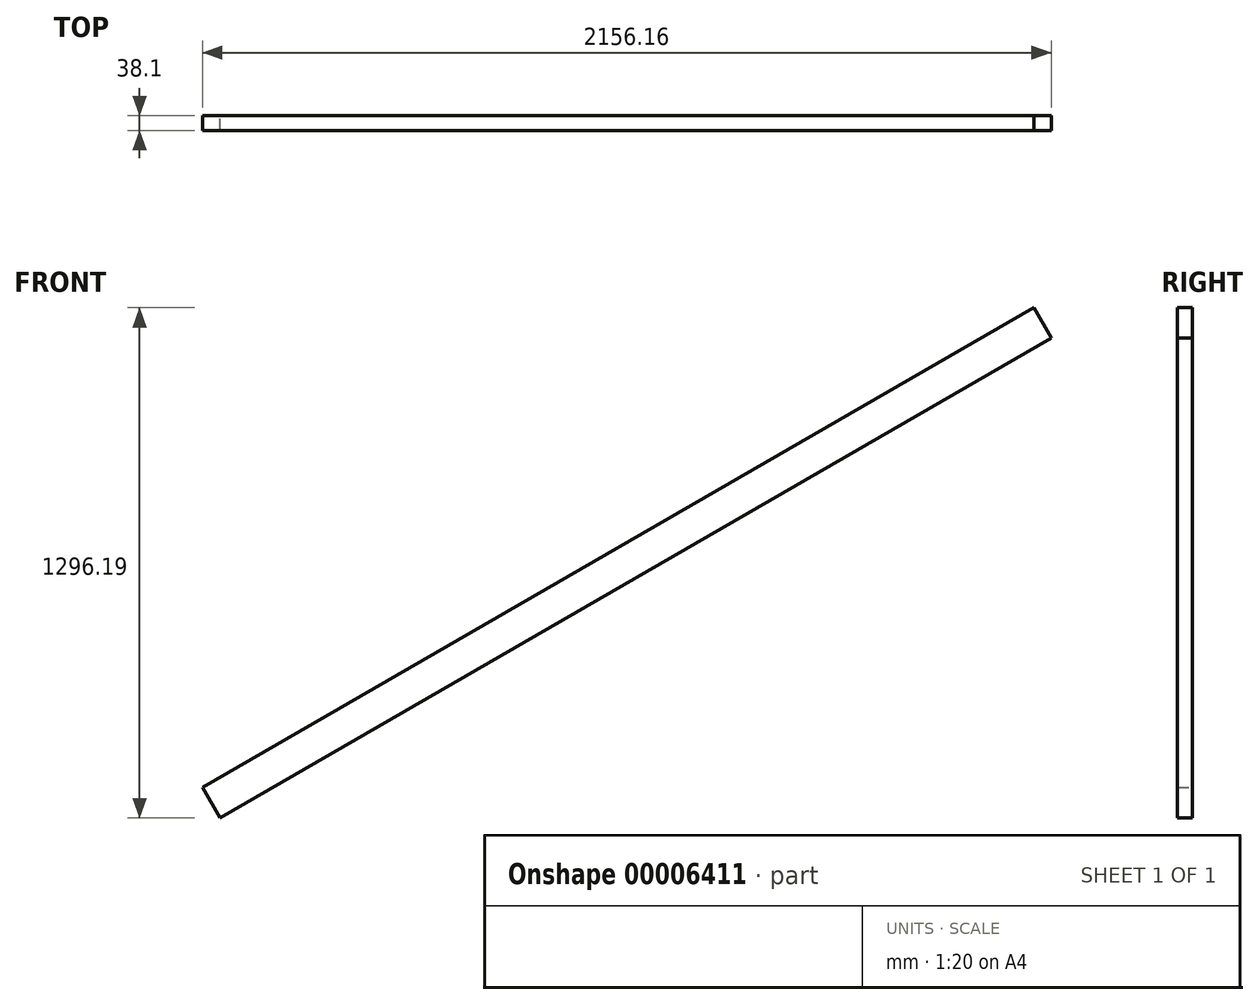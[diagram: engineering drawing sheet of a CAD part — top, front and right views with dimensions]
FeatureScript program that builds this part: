
annotation { "Feature Type Name" : "Feature", "Feature Type Description" : "" }
export const myFeature = defineFeature(function(context is Context, id is Id, definition is map)
    precondition{}
    {
        {
            var Q0;
            Q0=qCreatedBy(makeId("Front.planeOp"),FACE);
            var sketch = newSketch(context, id + "F0", { "sketchPlane" : qUnion([Q0])});
            skLineSegment(sketch, "E0", {"start": v(-1068.91, -542) * mm, "end": v(1042.8, 677.2) * mm});
            skLineSegment(sketch, "E1", {"start": v(1042.8, 677.2) * mm, "end": v(998.35, 754.2) * mm});
            skLineSegment(sketch, "E2", {"start": v(998.35, 754.2) * mm, "end": v(-1113.36, -465) * mm});
            skLineSegment(sketch, "E3", {"start": v(-1113.36, -465) * mm, "end": v(-1068.91, -542) * mm});
            skSolve(sketch);
        }
        {
            var Q0;
            Q0=makeQuery(id+"F0.imprint","IMPRINT",FACE,{"disambiguationData":[TD([[makeQuery(id+"F0.imprint","IMPRINT",EDGE,{"derivedFrom":sQuery(id+"F0.wireOp",EDGE,"E0")}),1.0]])]});
            extrude(context, id + "F1", {"entities" : qUnion([Q0]), "depth" : 38.1 * mm});
        }
    });
